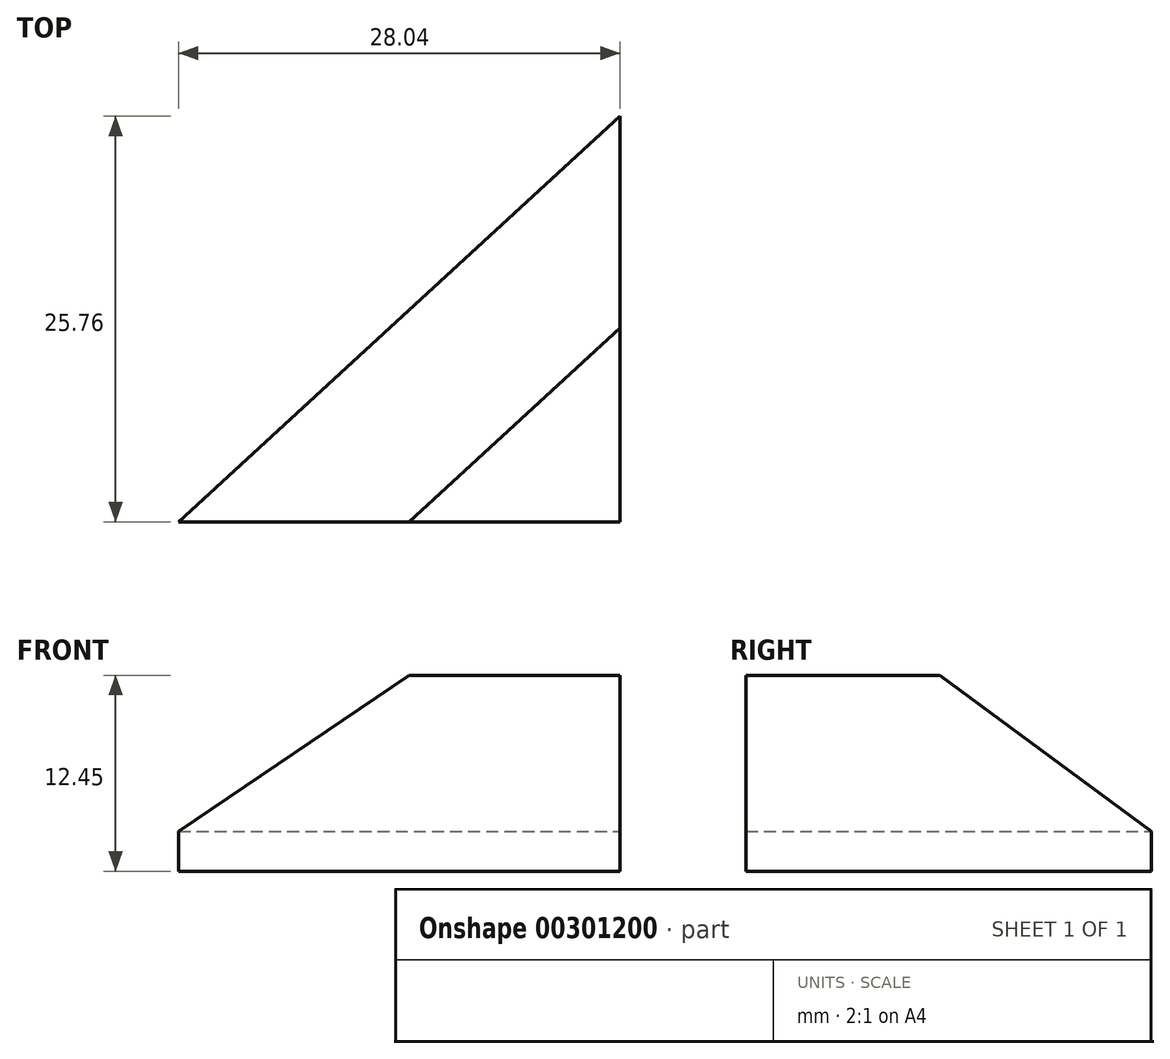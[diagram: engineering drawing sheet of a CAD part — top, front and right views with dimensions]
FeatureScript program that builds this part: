
annotation { "Feature Type Name" : "Feature", "Feature Type Description" : "" }
export const myFeature = defineFeature(function(context is Context, id is Id, definition is map)
    precondition{}
    {
        {
            var Q0;
            Q0=qCreatedBy(makeId("Top.planeOp"),FACE);
            var sketch = newSketch(context, id + "F0", { "sketchPlane" : qUnion([Q0])});
            skLineSegment(sketch, "E0", {"start": v(0, 0) * mm, "end": v(-28.04, 0) * mm});
            skLineSegment(sketch, "E1", {"start": v(-28.04, 0) * mm, "end": v(0, 25.76) * mm});
            skLineSegment(sketch, "E2", {"start": v(0, 25.76) * mm, "end": v(0, 0) * mm});
            skSolve(sketch);
        }
        {
            var Q0;
            Q0 = qSketchRegion(id + "F0", true);
            extrude(context, id + "F1", {"entities" : qUnion([Q0]), "depth" : 12.45 * mm});
        }
        {
            var Q0;
            Q0=makeQuery(id+"F1.opExtrude","CAP_EDGE",EDGE,{"disambiguationData":[OSD([sQuery(id+"F0.wireOp",EDGE,"E1")])],"isStart":false});
            chamfer(context, id + "F2", {"entities" : qUnion([Q0]), "width" : 9.9 * mm, "tangentPropagation" : true});
        }
    });
